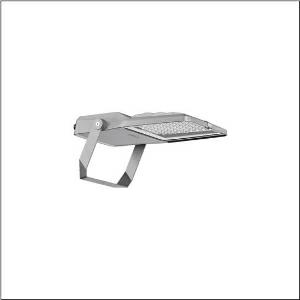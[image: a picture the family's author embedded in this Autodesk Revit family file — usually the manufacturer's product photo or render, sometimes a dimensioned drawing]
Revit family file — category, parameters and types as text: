
# Revit family: floodlight_fl_21_mini___pl64_5xa7772b4e1a_86d7
name_source: partatom
category: Lighting Fixtures
units: mm (PartAtom-declared; Revit-internal decimal feet)

## family parameters
Cut with Voids When Loaded = No
Host = Face
Light Source = No
Part Type = Normal
Room Calculation Point = No
Round Connector Dimension = Use Diameter
Shared = No

## types (1)
- --- (1 x LED, 6270 lm, 45.5 W, 4000K)
    Apparent Load = 46 VA
    CIE Flux Codes = 28 80 98 100 100
    Color Rendering = 70
    Color Temperature = 4000K
    Default Elevation = 1800 mm
    Description = Floodlight FL 21 mini, floodlight, primary light control with lens, of PMMA, primary optical cover: protective disc, of toughened safety glass, transparent, light distribution: PL64, light emission: direct distribution, installation type: surface-mounted, LED, High Power LED, rated luminous flux: 6.270lm, luminous efficacy: 138lm/W, light colour: 740, colour temperature: 4000K, control gear: ECG iQ, control: Street-Remote, Auto-Match, Temp-Guard, Night-Set, Smart-Wire, Desk-Remote (wireless, voltage-free reading and setting of iQ features in the workshop via application-optimized NFC function/RFID function), optimised constant luminous flux control (CLO 2.0), with terminal, 6-pole, mains connection: 220..240V, AC, 50/60Hz, start of lifetime: 46W, end of lifetime: 48W, reduction: 22W, luminaire housing, of diecast aluminium, powder-coated, Siteco® metallic grey (DB 702S), corrosivity category C5 according to DIN EN ISO 12944, mounting bracket, of steel, galvanised, powder-coated, Siteco® metallic grey (DB 702S), protection rating (complete): IP66, insulation class (complete): insulation class II (safety insulation), certification: CE, ENEC, VDE, protection symbol: D, impact resistance: IK08, permissible operating ambient temperature: -40..+40°C, permissible operating ambient temperature for outdoor applications: -40..+50°C, standard: DIN EN 12944, packaging unit: 1 piece

Light Distribution: PL64
    Height = 70 mm
    Lamp = 1 x LED
    Lamp Light Flux = 6270 lm
    Lamp Power = 45.5 W
    Lamp count = 1
    Length = 485 mm
    Luminous efficacy = 138 lm/W
    Manufacturer = Siteco
    ModVariant = No
    Model = 5XA7772B4E1A
    Number of Poles = 1
    OnlyDefault = Yes
    Power Factor = 1
    Product Name = Floodlight FL 21 mini | PL64
    Product group = floodlight | pylon top
    ProductGroupID = 6101
    Protection Class = Protection class II
    Protection Degree = IP 66
    RLX_Detail_Level = 1
    RlxData = <blob elided: 96081 chars, md5=06ac4842>
    Socket = socket
    Standby Power = 0 W
    System Light Flux = 6270 lm
    System Power = 46 W
    Type Comments = factory setting: luminous flux: 100 % | dim-lin: 254 | 463 mA
    Type Image = l_1006845.jpg
    URL = http://relux.com
    VarID = @adj_077881
    Voltage = 0 V
    Weight = 0.00 kg
    Width = 337 mm

## geometry (parser evidence)
native form markers: Blend x4, Sweep x14
no freeform markers — native parametric forms only
